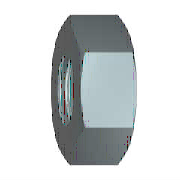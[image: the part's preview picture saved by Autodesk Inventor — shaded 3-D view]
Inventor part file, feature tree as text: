
AUTODESK INVENTOR PART (.ipt)
format: ipt  version: 2020 (Build 240168000, 168)  size: 166,400 bytes
history: native  units: mm (DEFAULTED — no unit token found)
features: sketch x3, chamfer x1, hole x1, other x1, plane x1
ambient origin geometry x7: Origin, YZ Plane, XZ Plane, X Axis, Y Axis, Z Axis, Center Point
bodies: Solid1 (feature_tree), Body (feature_tree)
feature tree (7):
  chamfer  "Chamfer1"  Angle=30.0deg  [1 undecoded]
  hole  "Thread"  [1 undecoded]
  other  "Work Axis1"
  plane  "Work Plane1"
  sketch  "Sketch1"  dims[d0=8.082904mm]
  sketch  "Sketch2"  dims[d1=3.2mm]
  sketch  "Sketch3"  dims[d2=0.0mm d3=30.0deg d4=30.0deg d5=5.9mm d6=5.9mm d7=90.0deg d25=3.242mm d26=6.0mm d27=4.0mm d28=2.0mm d29=14.3117mm d30=8.0mm d31=20.594885mm d8=0.378886mm d9=30.0deg d10=0.378886mm d11=30.0deg d13=0.0mm d14=0.0mm d39=0.0mm d40=0.378886mm d41=0.378886mm d42=0.0mm]
note: 2 required parameter values undecoded (feature->parameter linkage not recoverable at this tier; creation-order binding heuristic only, values carry confidence <= 0.55)
